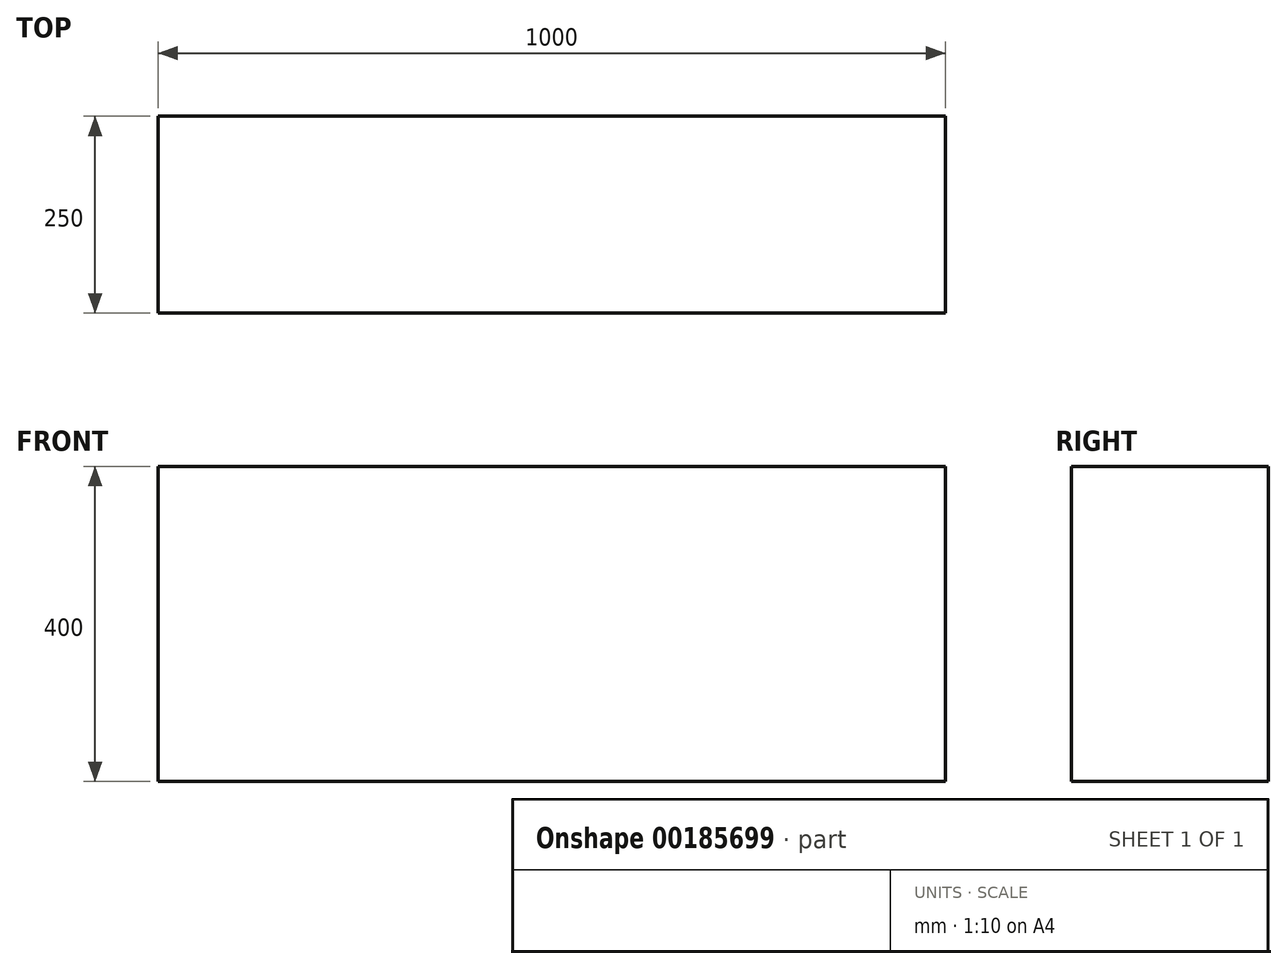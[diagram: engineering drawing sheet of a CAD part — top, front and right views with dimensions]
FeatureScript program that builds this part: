
annotation { "Feature Type Name" : "Feature", "Feature Type Description" : "" }
export const myFeature = defineFeature(function(context is Context, id is Id, definition is map)
    precondition{}
    {
        {
            var Q0;
            Q0=qCreatedBy(makeId("Top.planeOp"),FACE);
            var sketch = newSketch(context, id + "F0", { "sketchPlane" : qUnion([Q0])});
            skLineSegment(sketch, "E0.bottom", {"start": v(0, 0) * mm, "end": v(1000, 0) * mm});
            skLineSegment(sketch, "E0.top", {"start": v(0, 250) * mm, "end": v(1000, 250) * mm});
            skLineSegment(sketch, "E0.left", {"start": v(0, 0) * mm, "end": v(0, 250) * mm});
            skLineSegment(sketch, "E0.right", {"start": v(1000, 0) * mm, "end": v(1000, 250) * mm});
            skSolve(sketch);
        }
        {
            var Q0;
            Q0=makeQuery(id+"F0.imprint","IMPRINT",FACE,{"disambiguationData":[TD([[makeQuery(id+"F0.imprint","IMPRINT",EDGE,{"derivedFrom":sQuery(id+"F0.wireOp",EDGE,"E0.bottom")}),1.0]])]});
            extrude(context, id + "F1", {"entities" : qUnion([Q0]), "depth" : 400 * mm});
        }
    });
